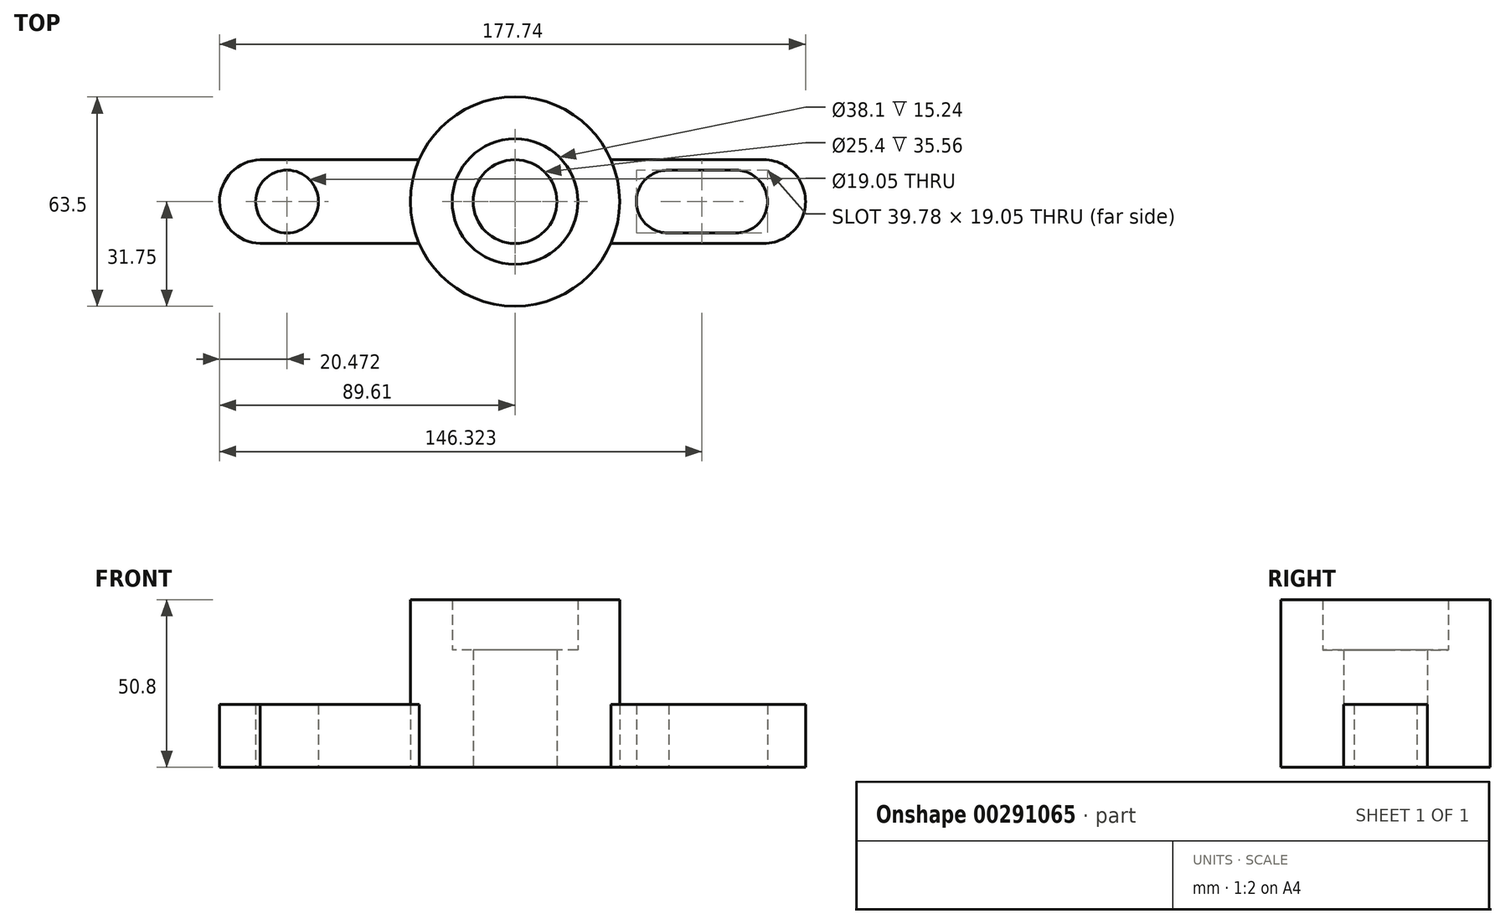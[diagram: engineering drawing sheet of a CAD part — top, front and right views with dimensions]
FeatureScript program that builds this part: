
annotation { "Feature Type Name" : "Feature", "Feature Type Description" : "" }
export const myFeature = defineFeature(function(context is Context, id is Id, definition is map)
    precondition{}
    {
        {
            var Q0;
            Q0=qCreatedBy(makeId("Top.planeOp"),FACE);
            var sketch = newSketch(context, id + "F0", { "sketchPlane" : qUnion([Q0])});
            skCircle(sketch, "E0", {"center": v(0, 0) * mm, "radius": 12.7 * mm});
            skCircle(sketch, "E1", {"center": v(0, 0) * mm, "radius": 19.05 * mm});
            skCircle(sketch, "E2", {"center": v(0, 0) * mm, "radius": 31.75 * mm});
            skArc(sketch, "E3", {"start": v(75.43, -12.7) * mm, "mid": v(88.13, 0) * mm, "end": v(75.43, 12.7) * mm});
            skArc(sketch, "E4", {"start": v(-76.59, 12.7) * mm, "mid": v(-89.61, 0) * mm, "end": v(-76.6, -12.7) * mm});
            skLineSegment(sketch, "E5", {"start": v(-77.24, 12.7) * mm, "end": v(-29.1, 12.7) * mm});
            skLineSegment(sketch, "E6", {"start": v(-77.23, -12.7) * mm, "end": v(-29.1, -12.7) * mm});
            skLineSegment(sketch, "E7.trimOffspring", {"start": v(-0.23, 12.7) * mm, "end": v(0.23, 12.7) * mm});
            skLineSegment(sketch, "E8.trimOffspring", {"start": v(29.1, 12.7) * mm, "end": v(75.43, 12.7) * mm});
            skLineSegment(sketch, "E9.trimOffspring", {"start": v(29.1, -12.7) * mm, "end": v(75.43, -12.7) * mm});
            skLineSegment(sketch, "E10.trimOffspring", {"start": v(-0.22, -12.7) * mm, "end": v(0.22, -12.7) * mm});
            skCircle(sketch, "E11", {"center": v(-69.14, 0) * mm, "radius": 9.53 * mm});
            skArc(sketch, "E12", {"start": v(67.08, -9.53) * mm, "mid": v(76.6, 0) * mm, "end": v(67.08, 9.52) * mm});
            skArc(sketch, "E13", {"start": v(46.66, 9.52) * mm, "mid": v(36.82, 0.16) * mm, "end": v(46.35, -9.53) * mm});
            skLineSegment(sketch, "E14", {"start": v(46.02, 9.52) * mm, "end": v(67.08, 9.52) * mm});
            skLineSegment(sketch, "E15", {"start": v(46.35, -9.53) * mm, "end": v(67.08, -9.53) * mm});
            skSolve(sketch);
        }
        {
            var Q0;
            Q0=makeQuery(id+"F0.imprint","IMPRINT",FACE,{"disambiguationData":[TD([[makeQuery(id+"F0.imprint","IMPRINT",EDGE,{"derivedFrom":sQuery(id+"F0.wireOp",EDGE,"E11")}),-1.0]])]});
            var Q1;
            Q1=makeQuery(id+"F0.imprint","IMPRINT",FACE,{"disambiguationData":[TD([[makeQuery(id+"F0.imprint","IMPRINT",EDGE,{"derivedFrom":sQuery(id+"F0.wireOp",EDGE,"E3")}),1.0]])]});
            extrude(context, id + "F1", {"entities" : qUnion([Q0, Q1]), "depth" : 19.05 * mm});
        }
        {
            var Q0;
            Q0=makeQuery(id+"F0.imprint","IMPRINT",FACE,{"disambiguationData":[TD([[makeQuery(id+"F0.imprint","IMPRINT",EDGE,{"derivedFrom":sQuery(id+"F0.wireOp",EDGE,"E1")}),-1.0]])]});
            extrude(context, id + "F2", {"entities" : qUnion([Q0]), "depth" : 50.8 * mm});
        }
        {
            var Q0;
            Q0=makeQuery(id+"F0.imprint","IMPRINT",FACE,{"disambiguationData":[TD([[makeQuery(id+"F0.imprint","IMPRINT",EDGE,{"derivedFrom":sQuery(id+"F0.wireOp",EDGE,"E1")}),1.0]])]});
            extrude(context, id + "F3", {"entities" : qUnion([Q0]), "operationType" : NewBodyOperationType.ADD, "depth" : 35.56 * mm});
        }
    });
